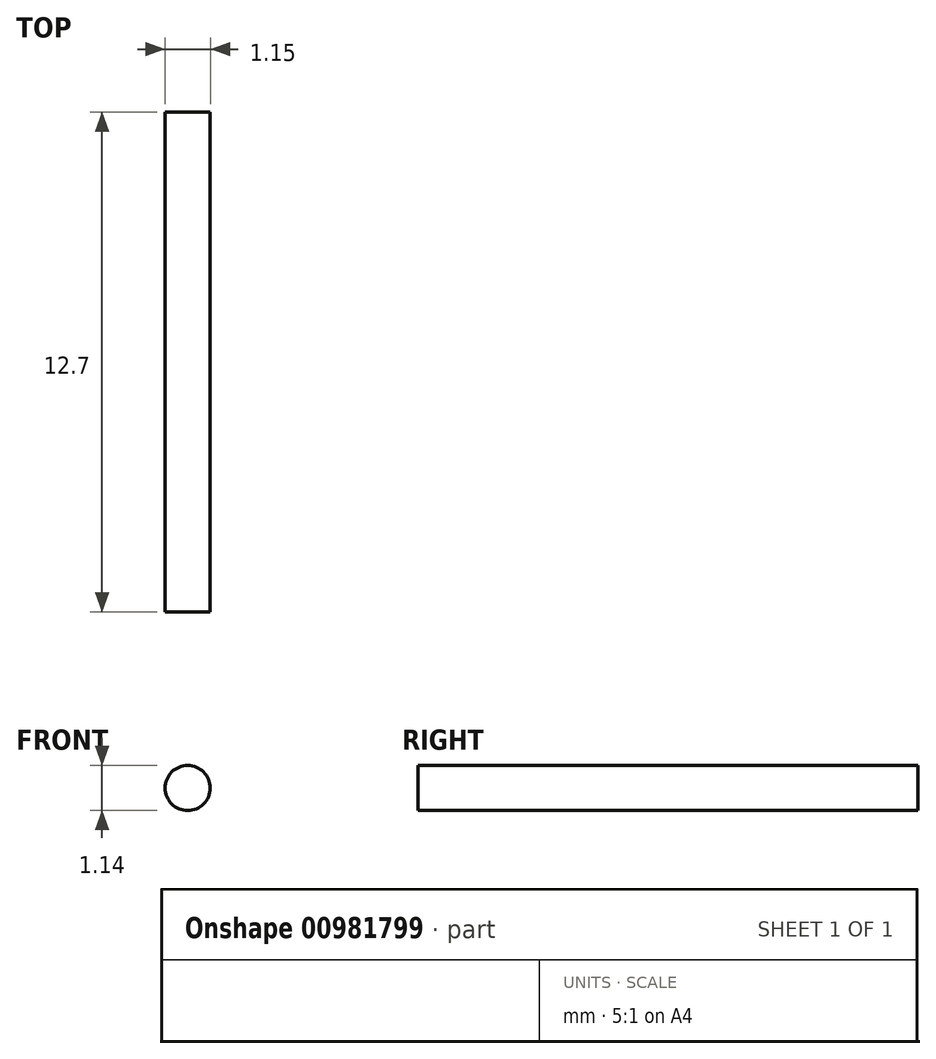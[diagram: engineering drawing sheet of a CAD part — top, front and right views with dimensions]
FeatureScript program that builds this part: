
annotation { "Feature Type Name" : "Feature", "Feature Type Description" : "" }
export const myFeature = defineFeature(function(context is Context, id is Id, definition is map)
    precondition{}
    {
        {
            var Q0;
            Q0=qCreatedBy(makeId("Front.planeOp"),FACE);
            var sketch = newSketch(context, id + "F0", { "sketchPlane" : qUnion([Q0])});
            skCircle(sketch, "E0", {"center": v(-12.67, 7.3) * mm, "radius": 0.57 * mm});
            skSolve(sketch);
        }
        {
            var Q0;
            Q0=makeQuery(id+"F0.imprint","IMPRINT",FACE,{"disambiguationData":[TD([[makeQuery(id+"F0.imprint","IMPRINT",EDGE,{"derivedFrom":sQuery(id+"F0.wireOp",EDGE,"E0")}),1.0]])]});
            extrude(context, id + "F1", {"entities" : qUnion([Q0]), "depth" : 12.7 * mm, "offsetDistance" : 25.4 * mm});
        }
    });
